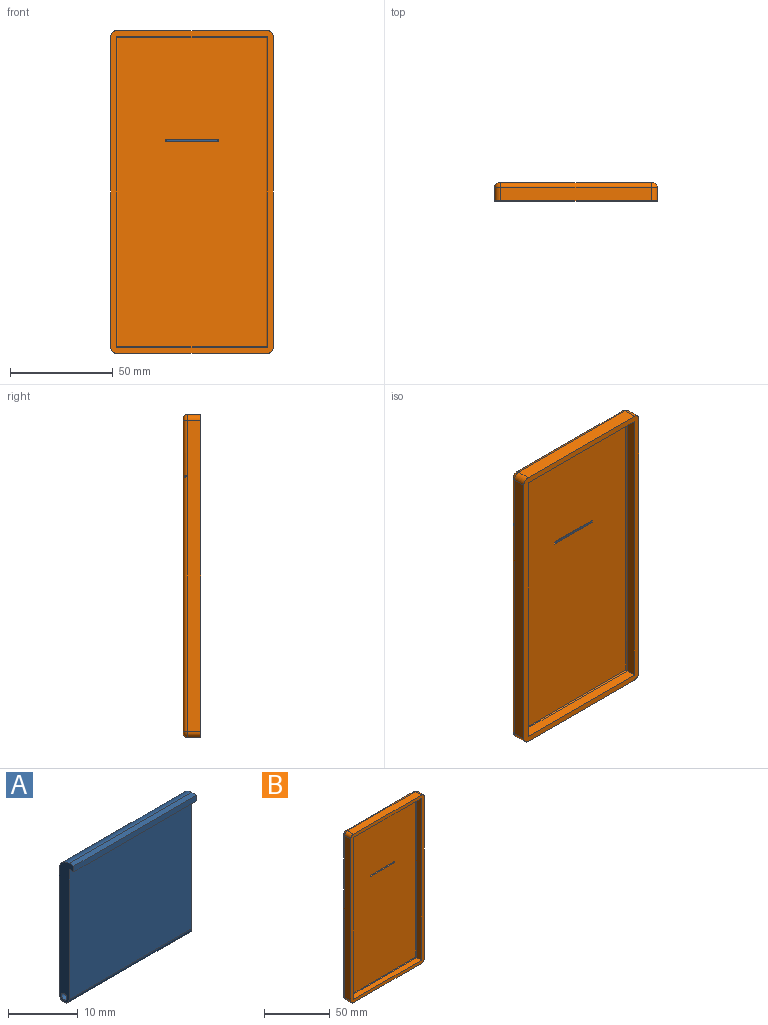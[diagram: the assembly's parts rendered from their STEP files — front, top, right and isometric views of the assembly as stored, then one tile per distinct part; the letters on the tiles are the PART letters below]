
ASSEMBLY  parts=2 mates=1
PART A: 10 faces, bbox 25x3x25 mm
  f0: plane 25x22mm, normal (0,1,0), area 550mm2, adj f5,f6,f7,f8
  f1: plane 25x1mm, normal (0,0,1), area 25mm2, adj f2,f5,f6,f8
  f2: plane 25x1mm, normal (0,-1,0), area 25mm2, adj f1,f3,f5,f6
  f3: plane 25x1mm, normal (0,0,-1), area 25mm2, adj f2,f4,f5,f6
  f4: plane 25x23mm, normal (0,-1,0), area 575mm2, adj f3,f5,f6,f7
  f5: plane 25x3mm, normal (1,0,0), area 48.8mm2, adj f0,f1,f2,f3,f4,f7,f8,f9
  f6: plane 25x3mm, normal (-1,0,0), area 48.8mm2, adj f0,f1,f2,f3,f4,f7,f8,f9
  f7: cylinder r=1mm len=25mm, axis (-1,0,0), area 78.5mm2, adj f0,f4,f5,f6
  f8: cylinder r=2mm len=25mm, axis (-1,0,0), area 78.5mm2, adj f0,f1,f5,f6
  f9: cylinder r=0.55mm len=25mm, axis (1,0,0), area 86.4mm2, adj f5,f6
PART B: 37 faces, bbox 79x8.5x157 mm
  f0: plane 150x72mm, normal (0,-1,0), area 10771.4mm2, adj f14,f15,f16,f17,f29,f30,f33,f34
  f1: plane 26x22.9mm, normal (0,1,0), area 595.4mm2, adj f29,f30,f35,f36
  f2: plane 153x75mm, normal (0,1,0), area 10460.1mm2, adj f4,f22,f23,f24,f25,f26,f27,f28
  f3: cylinder r=0.53mm len=26.44mm, axis (-1,0,0), area 86.3mm2, adj f4,f30
  f4: cylinder r=2mm len=151mm, axis (0,0,-1), area 473.4mm2, adj f2,f3,f7,f25,f28
  f5: plane 157x79mm, normal (0,-1,0), area 1372.3mm2, adj f6,f7,f8,f9,f10,f11,f12,f13
  f6: plane 73x6.5mm, normal (0,0,1), area 474.5mm2, adj f5,f18,f21,f27
  f7: plane 151x6.5mm, normal (-1,0,0), area 981.5mm2, adj f4,f5,f18,f19
  f8: plane 73x6.5mm, normal (0,0,-1), area 474.5mm2, adj f5,f19,f20,f23
  f9: plane 151x6.5mm, normal (1,0,0), area 981.5mm2, adj f5,f20,f21,f24
  f10: plane 73x5mm, normal (0,0,-1), area 365mm2, adj f5,f11,f13,f15
  f11: plane 151x5mm, normal (1,0,0), area 755mm2, adj f5,f10,f12,f14
  f12: plane 73x5mm, normal (0,0,1), area 365mm2, adj f5,f11,f13,f16
  f13: plane 151x5mm, normal (-1,0,0), area 755mm2, adj f5,f10,f12,f17
  f14: cylinder r=0.5mm len=151mm, axis (0,0,1), area 118.3mm2, adj f0,f11,f15,f16
  f15: cylinder r=0.5mm len=73mm, axis (1,0,0), area 57mm2, adj f0,f10,f14,f17
  f16: cylinder r=0.5mm len=73mm, axis (-1,0,0), area 57mm2, adj f0,f12,f14,f17
  f17: cylinder r=0.5mm len=151mm, axis (0,0,-1), area 118.3mm2, adj f0,f13,f15,f16
  f18: cylinder r=3mm len=6.5mm, axis (0,-1,0), area 30.6mm2, adj f5,f6,f7,f28
  f19: cylinder r=3mm len=6.5mm, axis (0,1,0), area 30.6mm2, adj f5,f7,f8,f25
  f20: cylinder r=3mm len=6.5mm, axis (0,-1,0), area 30.6mm2, adj f5,f8,f9,f22
  f21: cylinder r=3mm len=6.5mm, axis (0,1,0), area 30.6mm2, adj f5,f6,f9,f26
  f22: torus R=1mm, axis (0,-1,0), area 11.2mm2, adj f2,f20,f23,f24
  f23: cylinder r=2mm len=73mm, axis (1,0,0), area 229.3mm2, adj f2,f8,f22,f25
  f24: cylinder r=2mm len=151mm, axis (0,0,1), area 474.4mm2, adj f2,f9,f22,f26
  f25: torus R=1mm, axis (0,-1,0), area 11.2mm2, adj f2,f4,f19,f23
  f26: torus R=1mm, axis (0,-1,0), area 11.2mm2, adj f2,f21,f24,f27
  f27: cylinder r=2mm len=73mm, axis (-1,0,0), area 229.3mm2, adj f2,f6,f26,f28
  f28: torus R=1mm, axis (0,-1,0), area 11.2mm2, adj f2,f4,f18,f27
  f29: plane 39x3mm, normal (-1,0,0), area 70.6mm2, adj f0,f1,f2,f32,f33,f34,f35,f36
  f30: plane 39x3mm, normal (1,0,0), area 70.6mm2, adj f0,f1,f2,f3,f33,f34,f35,f36
  f31: cone r=0mm half-angle=59deg, axis (-1,0,0), area 1mm2, adj f32
  f32: cylinder r=0.53mm len=7.5mm, axis (-1,0,0), area 24.7mm2, adj f29,f31
  f33: plane 26x0.3mm, normal (0,0,-1), area 7.8mm2, adj f0,f29,f30,f35
  f34: cylinder r=3mm len=26mm, axis (-1,0,0), area 122.5mm2, adj f0,f2,f29,f30
  f35: plane 26x2mm, normal (0,0.97,-0.24), area 53.6mm2, adj f1,f29,f30,f33
  f36: plane 26x10mm, normal (0,0.98,-0.21), area 266.2mm2, adj f1,f2,f29,f30
PLACE A rot(axis=(0,1,0),180deg) t=(-6.65,4.14,50.26)mm
PLACE B t=(-6.65,4.14,0.76)mm fixed
MATE cylindrical B.f3 <-> A.f7  axis (-1,0,0) through (-32.95,3.14,49.26)mm
